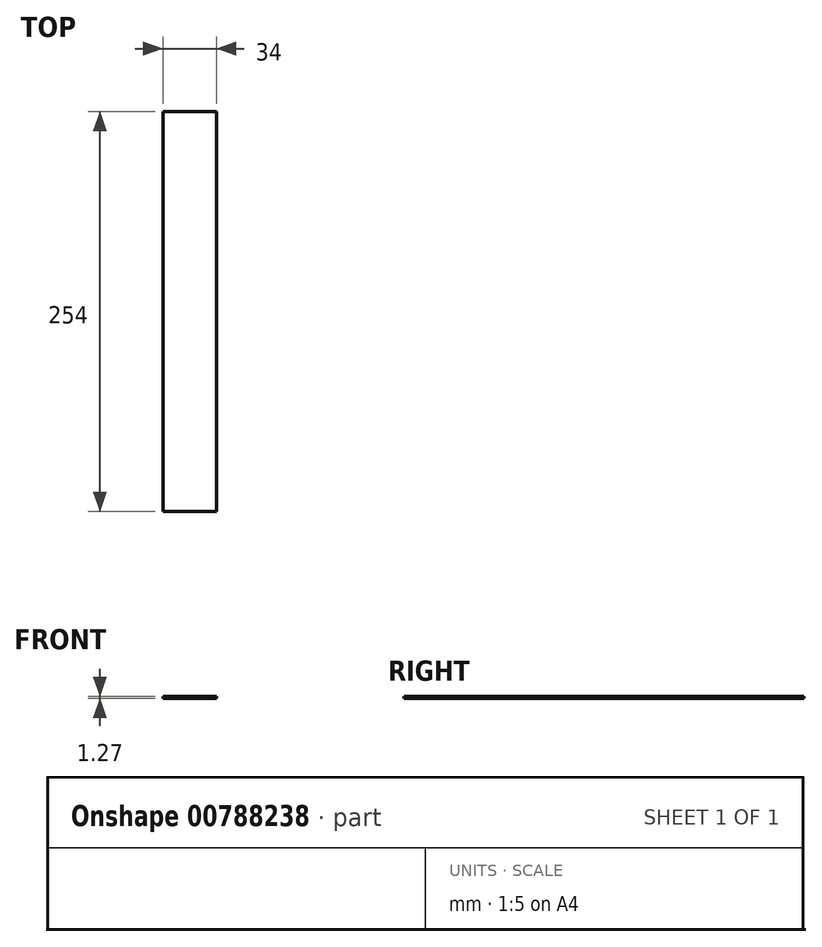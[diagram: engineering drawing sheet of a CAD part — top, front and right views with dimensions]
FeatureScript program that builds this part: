
annotation { "Feature Type Name" : "Feature", "Feature Type Description" : "" }
export const myFeature = defineFeature(function(context is Context, id is Id, definition is map)
    precondition{}
    {
        {
            var Q0;
            Q0=qCreatedBy(makeId("Top.planeOp"),FACE);
            var sketch = newSketch(context, id + "F0", { "sketchPlane" : qUnion([Q0])});
            skLineSegment(sketch, "E0", {"start": v(0, 0) * mm, "end": v(0, 254) * mm});
            skLineSegment(sketch, "E1", {"start": v(0, 254) * mm, "end": v(34, 254) * mm});
            skLineSegment(sketch, "E2", {"start": v(34, 254) * mm, "end": v(34, 0) * mm});
            skLineSegment(sketch, "E3", {"start": v(34, 0) * mm, "end": v(0, 0) * mm});
            skSolve(sketch);
        }
        {
            var Q0;
            Q0 = qSketchRegion(id + "F0", true);
            extrude(context, id + "F1", {"entities" : qUnion([Q0]), "depth" : 1.27 * mm, "offsetDistance" : 25.4 * mm});
        }
    });
